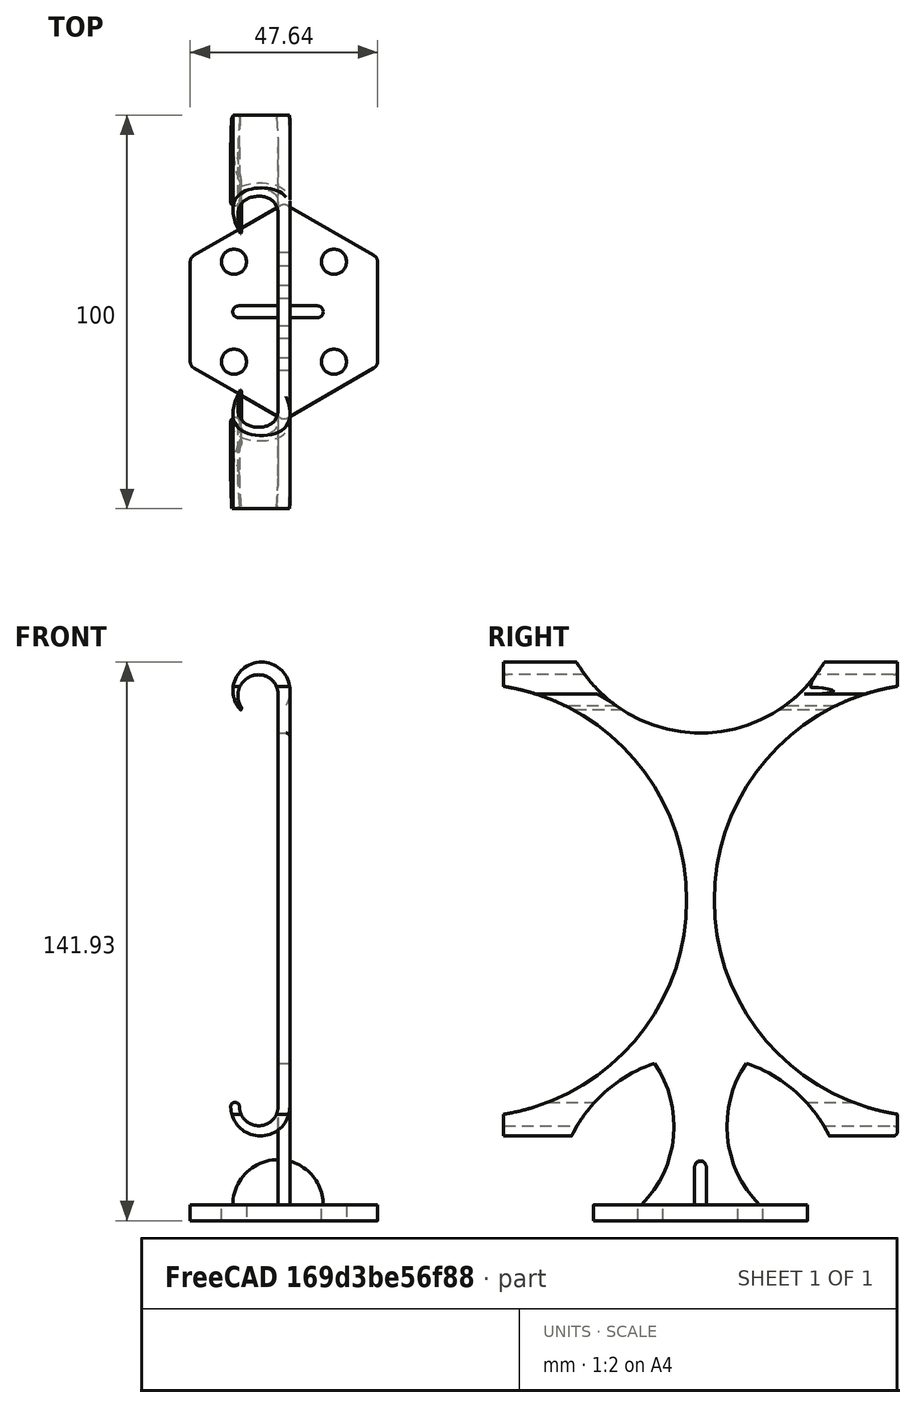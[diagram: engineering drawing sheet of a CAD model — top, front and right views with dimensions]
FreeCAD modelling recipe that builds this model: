
FCSTD DOCUMENT  (FreeCAD 0.19R24344 (Git))
Label: Holder_Tablet
Comment: First draft for a tablet holder. Ended up using a comercially available tablet holder instead.
License: Creative Commons Attribution-NonCommercial-ShareAlike
LicenseURL: http://creativecommons.org/licenses/by-nc-sa/4.0/
objects: PartDesign::Fillet×11, Sketcher::SketchObject×5, PartDesign::Pad×3, PartDesign::CoordinateSystem×2, PartDesign::Pocket×1, PartDesign::Revolution×1, PartDesign::Body×1
note: 40 computed .brp shape members not serialized (recipe doc carries the construction recipe); baked Part::Feature solids carry a one-line shape summary decoded from their .brp

FEATURE [Sketcher::SketchObject] Sketch
  FullyConstrained = true
  MapMode = 5
  Placement = pos=(0,0,0) rot=(1,0,0;1.5708rad)
  Support = -> [XZ_Plane]
  sketch-geometry (10):
    g0: LineSegment StartX=0 StartY=104.8 StartZ=0 EndX=0 EndY=0 EndZ=0
    g1: ArcOfCircle CenterX=-4.9 CenterY=104.8 CenterZ=0 NormalX=0 NormalY=0 NormalZ=1 AngleXU=0 Radius=4.9 StartAngle=1.3e-15 EndAngle=1.5708
    g2: ArcOfCircle CenterX=-4.9 CenterY=-1.25256e-05 CenterZ=0 NormalX=0 NormalY=0 NormalZ=1 AngleXU=0 Radius=4.9 StartAngle=3.14159 EndAngle=6.28319
    g3: LineSegment StartX=3 StartY=0 StartZ=0 EndX=3 EndY=104.8 EndZ=0
    g4: ArcOfCircle CenterX=-4.5 CenterY=0 CenterZ=0 NormalX=0 NormalY=0 NormalZ=1 AngleXU=0 Radius=7.5 StartAngle=3.14159 EndAngle=6.28319
    g5: ArcOfCircle CenterX=-4.9 CenterY=104.388 CenterZ=0 NormalX=0 NormalY=0 NormalZ=1 AngleXU=0 Radius=5.31162 StartAngle=1.5708 EndAngle=3.66519
    g6: ArcOfCircle CenterX=-4.19834 CenterY=105.681 CenterZ=0 NormalX=0 NormalY=0 NormalZ=1 AngleXU=0 Radius=7.25201 StartAngle=6.16144 EndAngle=10.1757
    g7: ArcOfCircle CenterX=-10.9 CenterY=-1e-16 CenterZ=0 NormalX=0 NormalY=0 NormalZ=1 AngleXU=0 Radius=1.1 StartAngle=1e-16 EndAngle=3.14159
    g8: ArcOfCircle CenterX=-10 CenterY=101.233 CenterZ=0 NormalX=0 NormalY=0 NormalZ=1 AngleXU=0 Radius=0.707107 StartAngle=5.49779 EndAngle=7.06858
    g9: LineSegment StartX=-4.9 StartY=-4.90001 StartZ=0 EndX=0.1 EndY=-4.90001 EndZ=0
  constraints (34):
    c: PointOnObject(g0,g-2)
    c: Coincident(g2,g0)
    c: Vertical(g3)
    c: Coincident(g4,g3)
    c: Horizontal(g2,g3)
    c: DistanceX(g2,g0) = 9.8
    c: Radius(g2) = 4.9
    c: Angle(g1) = 1.5708
    c: Radius(g1) = 4.9
    c: Tangent(g1,g0) = 1.5708
    c: DistanceX(g5,g0) = 9.5
    c: Tangent(g5,g1) = -1.5708
    c: DistanceX(g0,g3) = 3
    c: Coincident(g3,g6)
    c: Radius(g4) = 7.5
    c: Coincident(g7,g4)
    c: Coincident(g7,g2)
    c: Angle(g7) = 3.14159
    c: Horizontal(g4,g2)
    c: Horizontal(g2,g0)
    c: Angle(g4) = 3.14159
    c: Coincident(g8,g5)
    c: Coincident(g8,g6)
    c: Angle(g8) = 1.5708
    c: Vertical(g6,g5)
    c: Horizontal(g3,g0)
    c: Angle(g6) = 4.01426
    c: DistanceY(g6,g5) = 1
    c: Angle(g5) = 2.0944
    c: Coincident(g0,g-1)
    c: Horizontal(g9)
    c: Tangent(g9,g2) = -1.5708
    c: DistanceX(g9,g9) = 5
    c: DistanceY(g9,g1) = 114.6
FEATURE [PartDesign::Pad] Pad
  Direction = (1,1,1)
  Length = 100
  Length2 = 100
  Placement = pos=(0,0,0) rot=(1,0,0;1.5708rad)
  Profile = -> Sketch
  Type = 0
FEATURE [Sketcher::SketchObject] Sketch001
  ExternalGeometry = -> [Pad]
  FullyConstrained = true
  MapMode = 5
  Placement = pos=(3,0,0) rot=(0.707107,0,0.707107;3.14159rad)
  Support = -> [Pad]
  sketch-geometry (8):
    g0: Circle CenterX=52.4 CenterY=108.5 CenterZ=0 NormalX=0 NormalY=0 NormalZ=1 AngleXU=0 Radius=55
    g1: Circle CenterX=-23.6 CenterY=50 CenterZ=0 NormalX=0 NormalY=0 NormalZ=1 AngleXU=0 Radius=36.5
    g2: Circle CenterX=52.4 CenterY=-8.5 CenterZ=0 NormalX=0 NormalY=0 NormalZ=1 AngleXU=0 Radius=55
    g3: Circle CenterX=131.4 CenterY=50 CenterZ=0 NormalX=0 NormalY=0 NormalZ=1 AngleXU=0 Radius=36.5
    g4: LineSegment StartX=6.66e-14 StartY=100 StartZ=0 EndX=104.8 EndY=-7.11e-14 EndZ=0
    g5: LineSegment StartX=104.8 StartY=100 StartZ=0 EndX=0 EndY=0 EndZ=0
    g6: GeomPoint X=52.4 Y=50 Z=0
    g7: LineSegment StartX=-47.6 StartY=50 StartZ=0 EndX=152.4 EndY=50 EndZ=0
  constraints (21):
    c: Radius(g0) = 55
    c: Coincident(g4,g-3)
    c: Coincident(g4,g-4)
    c: Coincident(g5,g-3)
    c: Coincident(g5,g-1)
    c: PointOnObject(g6,g5)
    c: PointOnObject(g6,g4)
    c: Horizontal(g7)
    c: PointOnObject(g6,g7)
    c: Symmetric(g2,g0,g7)
    c: Equal(g2,g0)
    c: PointOnObject(g1,g7)
    c: Equal(g1,g3)
    c: PointOnObject(g3,g7)
    c: Radius(g1) = 36.5
    c: Vertical(g0,g6)
    c: DistanceX(g1,g6) = 76
    c: DistanceX(g6,g3) = 79
    c: DistanceX(g7,g7) = 200
    c: DistanceX(g7,g6) = 100
    c: DistanceY(g6,g0) = 58.5
FEATURE [PartDesign::Pocket] Pocket
  BaseFeature = -> Pad
  Length = 32
  Length2 = 100
  Midplane = true
  Placement = pos=(0,0,0) rot=(1,0,0;1.5708rad)
  Profile = -> Sketch001
  Type = 0
FEATURE [Sketcher::SketchObject] Sketch002
  FullyConstrained = true
  MapMode = 5
  Placement = pos=(3,0,0) rot=(0.707107,0,0.707107;3.14159rad)
  Support = -> [Pocket]
  sketch-geometry (4):
    g0: LineSegment StartX=15 StartY=65 StartZ=0 EndX=15 EndY=35 EndZ=0
    g1: LineSegment StartX=-25 StartY=35 StartZ=0 EndX=-25 EndY=65 EndZ=0
    g2: ArcOfCircle CenterX=-5 CenterY=85 CenterZ=0 NormalX=0 NormalY=0 NormalZ=1 AngleXU=0 Radius=28.2843 StartAngle=3.92699 EndAngle=5.49779
    g3: ArcOfCircle CenterX=-5 CenterY=15 CenterZ=0 NormalX=0 NormalY=0 NormalZ=1 AngleXU=0 Radius=28.2843 StartAngle=0.785398 EndAngle=2.35619
  constraints (14):
    c: Vertical(g0)
    c: Vertical(g1)
    c: DistanceY(g1,g1) = 30
    c: DistanceX(g1,g0) = 40
    c: Coincident(g2,g1)
    c: Coincident(g2,g0)
    c: Coincident(g3,g1)
    c: Coincident(g3,g0)
    c: DistanceX(g-1,g0) = 15
    c: DistanceY(g-1,g0) = 35
    c: Horizontal(g1,g0)
    c: Horizontal(g1,g0)
    c: Angle(g2) = 1.5708
    c: Angle(g3) = 1.5708
FEATURE [PartDesign::Pad] Pad001
  BaseFeature = -> Pocket
  Direction = (1,1,1)
  Length = 3
  Length2 = 100
  Placement = pos=(0,0,0) rot=(1,0,0;1.5708rad)
  Profile = -> Sketch002
  Reversed = true
  Type = 0
FEATURE [Sketcher::SketchObject] Sketch003
  ExternalGeometry = -> [Pad001]
  FullyConstrained = true
  MapMode = 5
  Placement = pos=(-5.5e-15,-5.5e-15,-25) rot=(1,0,0;3.14159rad)
  Support = -> [Pad001]
  sketch-geometry (16):
    g0: LineSegment StartX=25.3157 StartY=36.25 StartZ=0 EndX=25.3157 EndY=63.75 EndZ=0
    g1: LineSegment StartX=25.3157 StartY=63.75 StartZ=0 EndX=1.5 EndY=77.5 EndZ=0
    g2: LineSegment StartX=1.5 StartY=77.5 StartZ=0 EndX=-22.3157 EndY=63.75 EndZ=0
    g3: LineSegment StartX=-22.3157 StartY=63.75 StartZ=0 EndX=-22.3157 EndY=36.25 EndZ=0
    g4: LineSegment StartX=-22.3157 StartY=36.25 StartZ=0 EndX=1.5 EndY=22.5 EndZ=0
    g5: LineSegment StartX=1.5 StartY=22.5 StartZ=0 EndX=25.3157 EndY=36.25 EndZ=0
    g6: Circle CenterX=1.5 CenterY=50 CenterZ=0 NormalX=0 NormalY=0 NormalZ=1 AngleXU=0 Radius=27.5
    g7: Circle CenterX=-11.2 CenterY=62.7 CenterZ=0 NormalX=0 NormalY=0 NormalZ=1 AngleXU=0 Radius=3.2
    g8: Circle CenterX=-11.2 CenterY=37.3 CenterZ=0 NormalX=0 NormalY=0 NormalZ=1 AngleXU=0 Radius=3.2
    g9: Circle CenterX=14.2 CenterY=37.3 CenterZ=0 NormalX=0 NormalY=0 NormalZ=1 AngleXU=0 Radius=3.2
    g10: Circle CenterX=14.2 CenterY=62.7 CenterZ=0 NormalX=0 NormalY=0 NormalZ=1 AngleXU=0 Radius=3.2
    g11: LineSegment StartX=-4e-16 StartY=65 StartZ=0 EndX=3 EndY=35 EndZ=0
    g12: LineSegment StartX=3 StartY=65 StartZ=0 EndX=-4e-16 EndY=35 EndZ=0
    g13: GeomPoint X=1.5 Y=50 Z=0
    g14: LineSegment StartX=-18.5 StartY=50 StartZ=0 EndX=21.5 EndY=50 EndZ=0
    g15: LineSegment StartX=1.5 StartY=70 StartZ=0 EndX=1.5 EndY=30 EndZ=0
  constraints (38):
    c: Coincident(g0,g1)
    c: Coincident(g1,g2)
    c: Coincident(g2,g3)
    c: Coincident(g3,g4)
    c: Coincident(g4,g5)
    c: Coincident(g5,g0)
    c: Equal(g0, g1-g5) x5
    c: PointOnObject(g0,g6)
    c: PointOnObject(g1,g6)
    c: PointOnObject(g2,g6)
    c: PointOnObject(g3,g6)
    c: PointOnObject(g4,g6)
    c: Vertical(g0)
    c: Diameter(g7) = 6.4
    c: Equal(g7,g10)
    c: Equal(g8,g7)
    c: Equal(g9,g7)
    c: DistanceX(g7,g10) = 25.4
    c: DistanceY(g8,g7) = 25.4
    c: DistanceX(g8,g9) = 25.4
    c: DistanceY(g9,g10) = 25.4
    c: DistanceY(g4,g1) = 55
    c: Coincident(g11,g-3)
    c: Coincident(g11,g-4)
    c: Coincident(g12,g-3)
    c: Coincident(g12,g-4)
    c: PointOnObject(g13,g11)
    c: PointOnObject(g13,g12)
    c: DistanceY(g15,g15) = 40
    c: DistanceX(g14,g14) = 40
    c: PointOnObject(g13,g14)
    c: PointOnObject(g13,g15)
    c: Symmetric(g7,g10,g15)
    c: Symmetric(g10,g9,g14)
    c: Symmetric(g0,g2,g15)
    c: Symmetric(g0,g0,g14)
    c: Symmetric(g14,g14,g15)
    c: Symmetric(g15,g15,g14)
FEATURE [PartDesign::Pad] Pad002
  BaseFeature = -> Pad001
  Direction = (1,1,1)
  Length = 4
  Length2 = 100
  Placement = pos=(0,0,0) rot=(1,0,0;1.5708rad)
  Profile = -> Sketch003
  Type = 0
FEATURE [Sketcher::SketchObject] Sketch004
  FullyConstrained = true
  MapMode = 5
  Placement = pos=(-5.5e-15,-1.07e-14,-25) rot=(0,0,1;3.14159rad)
  Support = -> [Pad002]
  sketch-geometry (4):
    g0: LineSegment StartX=-10 StartY=51.5 StartZ=0 EndX=0 EndY=51.5 EndZ=0
    g1: LineSegment StartX=0 StartY=48.5 StartZ=0 EndX=-10 EndY=48.5 EndZ=0
    g2: ArcOfCircle CenterX=-10 CenterY=50 CenterZ=0 NormalX=0 NormalY=0 NormalZ=1 AngleXU=0 Radius=1.5 StartAngle=1.5708 EndAngle=4.71239
    g3: LineSegment StartX=0 StartY=51.5 StartZ=0 EndX=0 EndY=48.5 EndZ=0
  constraints (13):
    c: PointOnObject(g0,g-2)
    c: Horizontal(g0)
    c: PointOnObject(g1,g-2)
    c: Horizontal(g1)
    c: Coincident(g2,g1)
    c: Coincident(g2,g0)
    c: Angle(g2) = 3.14159
    c: DistanceY(g1,g0) = 3
    c: DistanceX(g0,g0) = 10
    c: Vertical(g1,g0)
    c: DistanceY(g-1,g2) = 50
    c: Coincident(g3,g0)
    c: Coincident(g3,g1)
FEATURE [PartDesign::Revolution] Revolution
  Angle = 180
  Axis = (0,-1,9e-16)
  Base = (-5.6e-15,-2.19e-14,-25)
  BaseFeature = -> Pad002
  Placement = pos=(0,0,0) rot=(1,0,0;1.5708rad)
  Profile = -> Sketch004
  ReferenceAxis = -> Sketch004 [V_Axis]
FEATURE [PartDesign::Fillet] Fillet
  Base = -> Revolution [Edge38]
  BaseFeature = -> Revolution
  Placement = pos=(0,0,0) rot=(1,0,0;1.5708rad)
  Radius = 2
  SupportTransform = false
FEATURE [PartDesign::Fillet] Fillet001
  Base = -> Fillet [Edge25]
  BaseFeature = -> Fillet
  Placement = pos=(0,0,0) rot=(1,0,0;1.5708rad)
  Radius = 2
  SupportTransform = false
FEATURE [PartDesign::Fillet] Fillet002
  Base = -> Fillet001 [Edge32]
  BaseFeature = -> Fillet001
  Placement = pos=(0,0,0) rot=(1,0,0;1.5708rad)
  Radius = 2
  SupportTransform = false
FEATURE [PartDesign::Fillet] Fillet003
  Base = -> Fillet002 [Edge33]
  BaseFeature = -> Fillet002
  Placement = pos=(0,0,0) rot=(1,0,0;1.5708rad)
  Radius = 2
  SupportTransform = false
FEATURE [PartDesign::Fillet] Fillet004
  Base = -> Fillet003 [Edge34]
  BaseFeature = -> Fillet003
  Placement = pos=(0,0,0) rot=(1,0,0;1.5708rad)
  Radius = 2
  SupportTransform = false
FEATURE [PartDesign::Fillet] Fillet005
  Base = -> Fillet004 [Edge35]
  BaseFeature = -> Fillet004
  Placement = pos=(0,0,0) rot=(1,0,0;1.5708rad)
  Radius = 2
  SupportTransform = false
FEATURE [PartDesign::Fillet] Fillet006
  Base = -> Fillet005 [Edge124]
  BaseFeature = -> Fillet005
  Placement = pos=(0,0,0) rot=(1,0,0;1.5708rad)
  Radius = 1
  SupportTransform = false
FEATURE [PartDesign::Fillet] Fillet007
  Base = -> Fillet006 [Edge38]
  BaseFeature = -> Fillet006
  Placement = pos=(0,0,0) rot=(1,0,0;1.5708rad)
  Radius = 1
  SupportTransform = false
FEATURE [PartDesign::Fillet] Fillet008
  Base = -> Fillet007 [Edge60]
  BaseFeature = -> Fillet007
  Placement = pos=(0,0,0) rot=(1,0,0;1.5708rad)
  Radius = 1
  SupportTransform = false
FEATURE [PartDesign::Fillet] Fillet009
  Base = -> Fillet008 [Edge96]
  BaseFeature = -> Fillet008
  Placement = pos=(0,0,0) rot=(1,0,0;1.5708rad)
  Radius = 1
  SupportTransform = false
FEATURE [PartDesign::Fillet] Fillet010
  Base = -> Fillet009 [Edge37]
  BaseFeature = -> Fillet009
  Placement = pos=(0,0,0) rot=(1,0,0;1.5708rad)
  Radius = 1
  SupportTransform = false
FEATURE [PartDesign::CoordinateSystem] LCS_Base
  AttacherType = Attacher::AttachEngine3D
  MapMode = 45
  Placement = pos=(-11.2,-37.3,-29) rot=(0,0,1;0rad)
  Support = -> [Fillet010]
FEATURE [PartDesign::CoordinateSystem] LCS_Tablet
  AttacherType = Attacher::AttachEngine3D
  MapMode = 45
  Placement = pos=(0,-50,57.518) rot=(0.57735,0.57735,0.57735;2.0944rad)
  Support = -> [Fillet010]
FEATURE [PartDesign::Body] Body  label="FireHolder"
  Group = -> [Sketch,Pad,Sketch001,Pocket,Sketch002,Pad001,Sketch003,Pad002,Sketch004,Revolution,Fillet,Fillet001,Fillet002,Fillet003,Fillet004,Fillet005,Fillet006,Fillet007,Fillet008,Fillet009,Fillet010,LCS_Base,LCS_Tablet]
  Origin = -> Origin
  Tip = -> Fillet010
